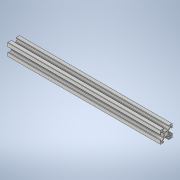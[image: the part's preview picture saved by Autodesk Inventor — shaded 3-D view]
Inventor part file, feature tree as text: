
AUTODESK INVENTOR PART (.ipt)
format: ipt  version: 2020 (Build 240168000, 168)  size: 262,656 bytes
history: mixed  units: mm
features: sketch x3, other x2, extrude x1, imported_body x1
ambient origin geometry x8: Origin, YZ Plane, XZ Plane, XY Plane, X Axis, Y Axis, Z Axis, Center Point
bodies: Body1 (imported_parasolid)
feature tree (7):
  other  "Sólido1"
  extrude  "Extrusión1"  Depth=250.0mm
  sketch  "Boceto3"
  sketch  "Boceto7"
  sketch  "Boceto1"  dims[d0=150.0mm d1=0.0mm d8=250.0mm]
  other  "Quadrado PF20-01 - PERFIL 2020 BÁSICO(1)"
  imported_body  NMx_Import_Brep_tag  [imported B-rep: ~59 faces, bbox_mm=[250.0, 20.0, 20.0]]
